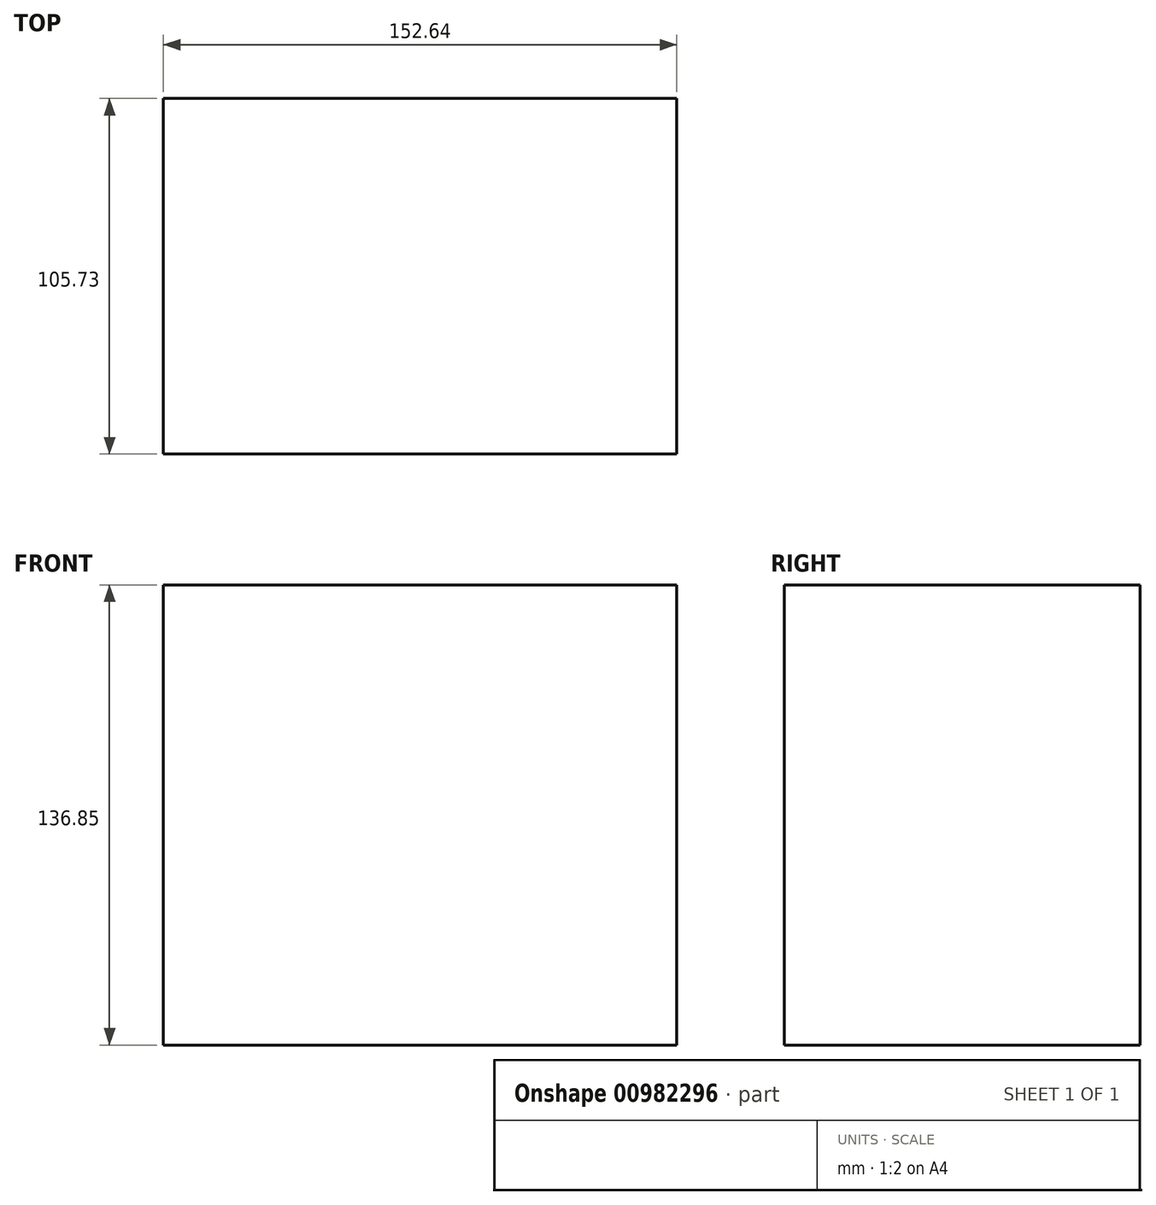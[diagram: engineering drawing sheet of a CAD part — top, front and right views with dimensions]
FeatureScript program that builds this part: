
annotation { "Feature Type Name" : "Feature", "Feature Type Description" : "" }
export const myFeature = defineFeature(function(context is Context, id is Id, definition is map)
    precondition{}
    {
        {
            var Q0;
            Q0=qCreatedBy(makeId("Front.planeOp"),FACE);
            var sketch = newSketch(context, id + "F0", { "sketchPlane" : qUnion([Q0])});
            skLineSegment(sketch, "E0.bottom", {"start": v(-42.27, 23.17) * mm, "end": v(110.37, 23.17) * mm});
            skLineSegment(sketch, "E0.top", {"start": v(-42.27, -113.68) * mm, "end": v(110.37, -113.68) * mm});
            skLineSegment(sketch, "E0.left", {"start": v(-42.27, 23.17) * mm, "end": v(-42.27, -113.68) * mm});
            skLineSegment(sketch, "E0.right", {"start": v(110.37, 23.17) * mm, "end": v(110.37, -113.68) * mm});
            skSolve(sketch);
        }
        {
            var Q0;
            Q0 = qSketchRegion(id + "F0", true);
            extrude(context, id + "F1", {"entities" : qUnion([Q0]), "depth" : 105.73 * mm, "offsetDistance" : 25.4 * mm});
        }
    });
